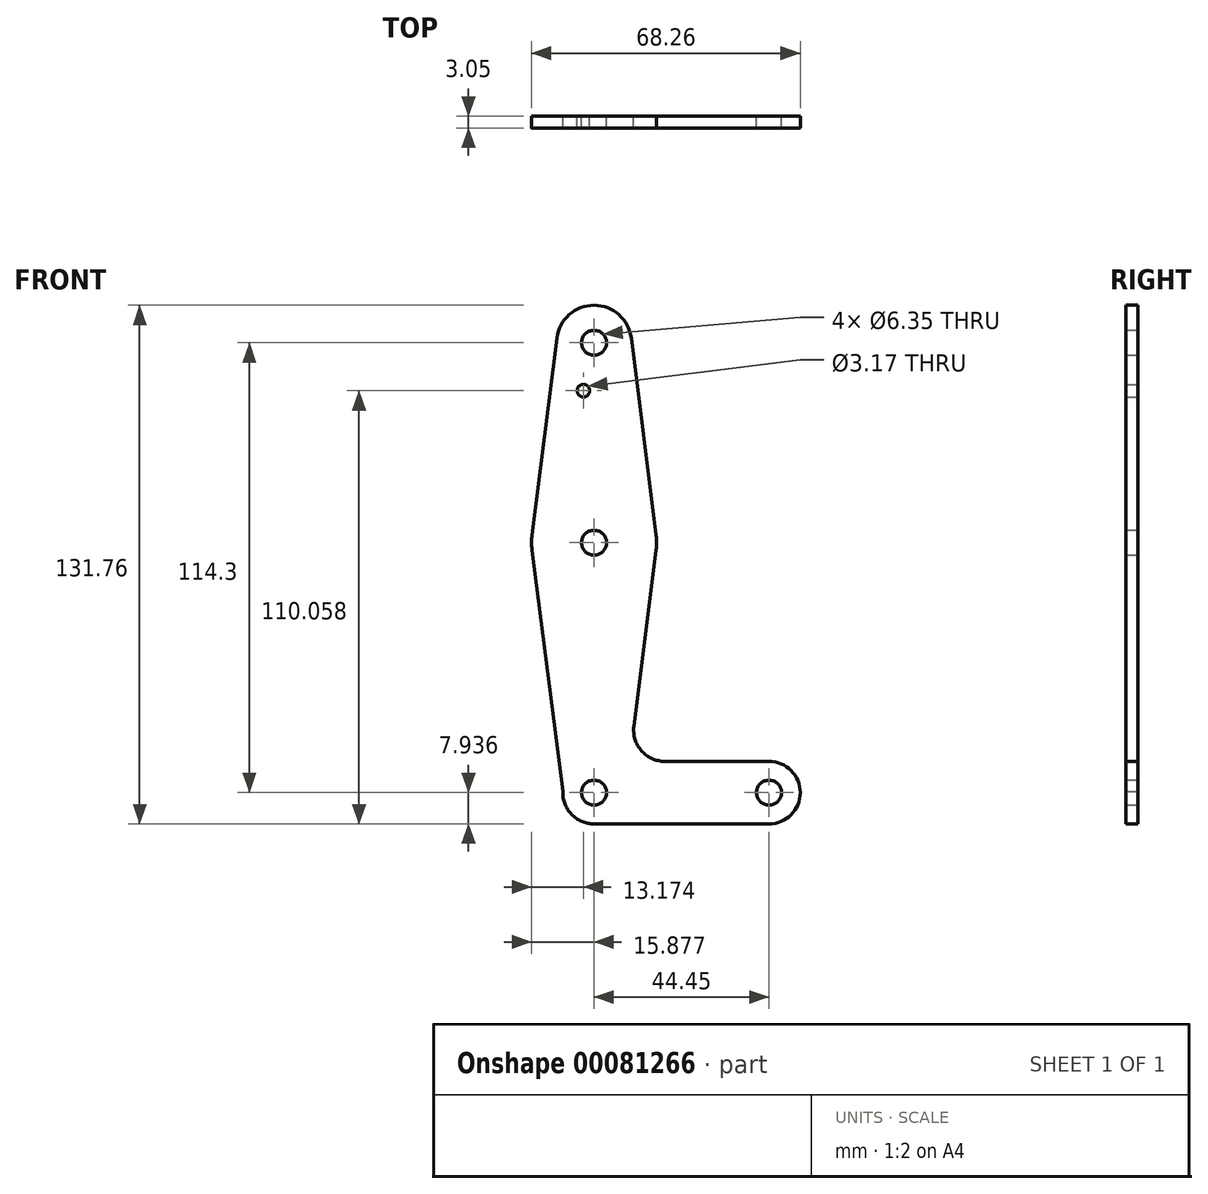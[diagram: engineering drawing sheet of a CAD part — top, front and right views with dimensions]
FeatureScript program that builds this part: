
annotation { "Feature Type Name" : "Feature", "Feature Type Description" : "" }
export const myFeature = defineFeature(function(context is Context, id is Id, definition is map)
    precondition{}
    {
        {
            var Q0;
            Q0=qCreatedBy(makeId("Front.planeOp"),FACE);
            var sketch = newSketch(context, id + "F0", { "sketchPlane" : qUnion([Q0])});
            skCircle(sketch, "E0", {"center": v(-45.3, 62.22) * mm, "radius": 9.53 * mm});
            skCircle(sketch, "E1", {"center": v(-45.3, 11.42) * mm, "radius": 15.88 * mm});
            skCircle(sketch, "E2", {"center": v(-45.3, -52.08) * mm, "radius": 7.94 * mm});
            skCircle(sketch, "E3", {"center": v(-0.85, -52.08) * mm, "radius": 7.94 * mm});
            skLineSegment(sketch, "E4", {"start": v(-54.75, 63.4) * mm, "end": v(-61.05, 13.4) * mm});
            skLineSegment(sketch, "E5", {"start": v(-29.55, 13.4) * mm, "end": v(-35.85, 63.4) * mm});
            skLineSegment(sketch, "E6", {"start": v(-45.3, -60.02) * mm, "end": v(0, -60.02) * mm});
            skLineSegment(sketch, "E7", {"start": v(-53.24, -51.8) * mm, "end": v(-61.05, 9.4) * mm});
            skLineSegment(sketch, "E8", {"start": v(-29.55, 9.43) * mm, "end": v(-35.18, -35.2) * mm});
            skLineSegment(sketch, "E9", {"start": v(-27.29, -44.15) * mm, "end": v(0, -44.15) * mm});
            skCircle(sketch, "E10", {"center": v(-45.3, 62.22) * mm, "radius": 3.18 * mm});
            skCircle(sketch, "E11", {"center": v(-45.3, 11.42) * mm, "radius": 3.18 * mm});
            skCircle(sketch, "E12", {"center": v(-45.3, -52.08) * mm, "radius": 3.18 * mm});
            skCircle(sketch, "E13", {"center": v(-0.85, -52.08) * mm, "radius": 3.18 * mm});
            skArc(sketch, "E14.filletArc", {"start": v(-35.18, -35.2) * mm, "mid": v(-33.25, -41.45) * mm, "end": v(-27.29, -44.15) * mm});
            skCircle(sketch, "E15", {"center": v(-48, 50.04) * mm, "radius": 1.59 * mm});
            skSolve(sketch);
        }
        {
            var Q0;
            Q0 = qSketchRegion(id + "F0", true);
            extrude(context, id + "F1", {"entities" : qUnion([Q0]), "depth" : 3.05 * mm});
        }
    });
